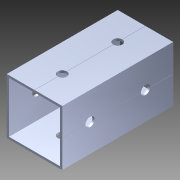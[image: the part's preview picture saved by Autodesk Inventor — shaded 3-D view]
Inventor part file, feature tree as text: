
AUTODESK INVENTOR PART (.ipt)
format: ipt  version: 2014 (Build 180170000, 170)  size: 1,123,328 bytes
history: native  units: in
note: dims shown in document units (in); Inventor stores cm internally (conversion verified against a paired STEP export)
features: pattern_circular x1, other x1, plane x1, extrude x1, imported_body x1, sketch x1
ambient origin geometry x8: Origin, YZ Plane, XZ Plane, XY Plane, X Axis, Y Axis, Z Axis, Center Point
bodies: Body1 (feature_tree)
feature tree (6):
  pattern_circular  "CirPattern2"
  other  "217-3426-STEP1"
  plane  "Work Plane1"
  extrude  "Extrusion1"  Depth=3937.0079in TaperAngle=0.0deg
  imported_body  "Base1"
  sketch  "Sketch1"  dims[d0=-2.0in d1=3937.0079in d2=0.0in]
